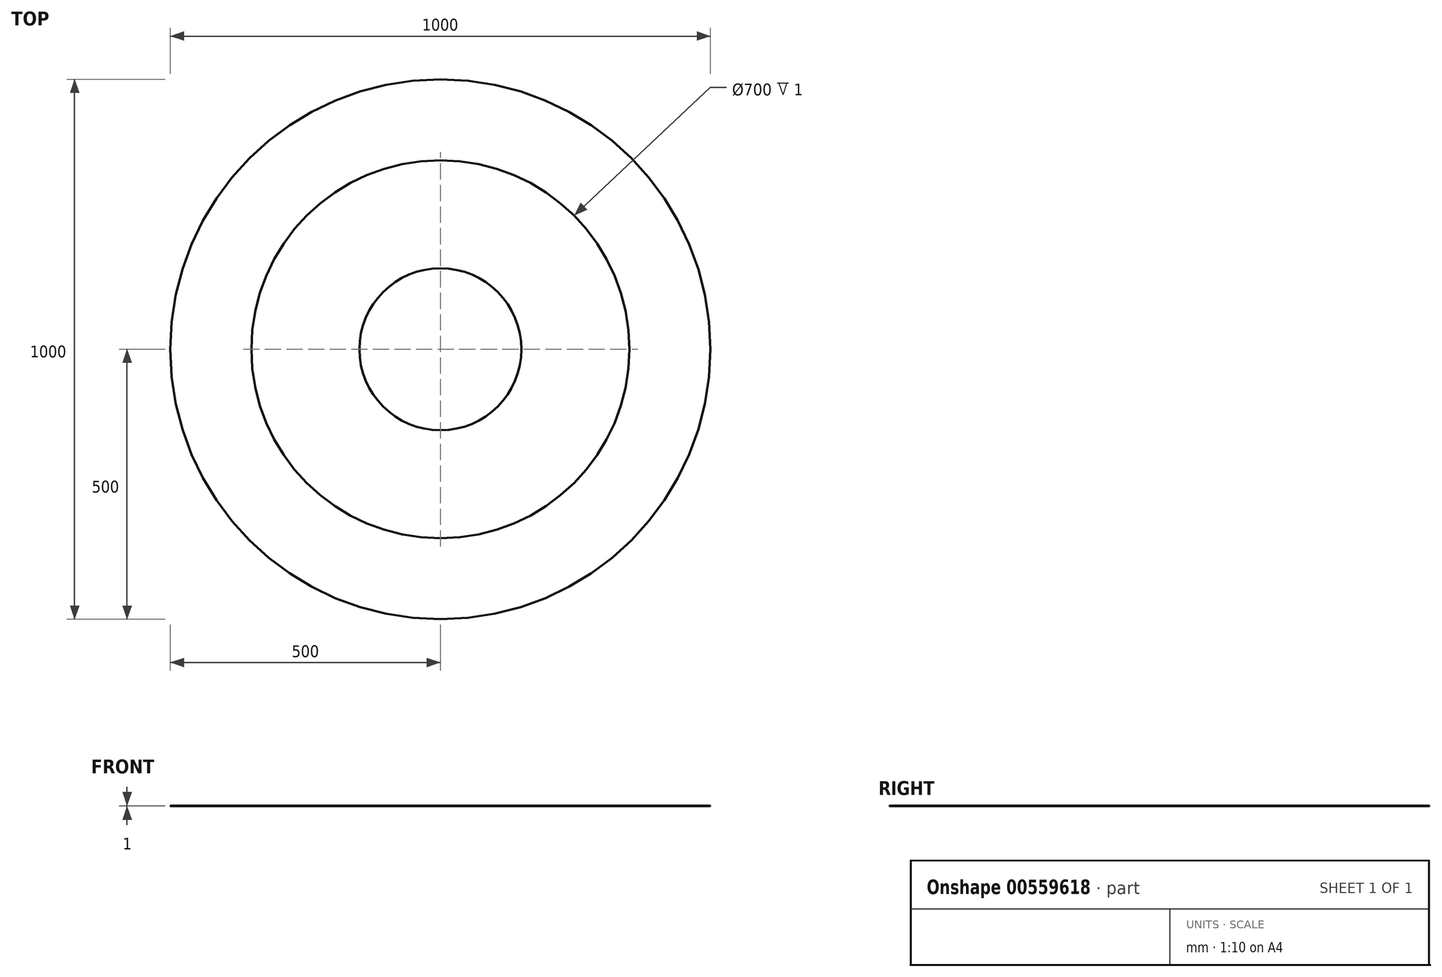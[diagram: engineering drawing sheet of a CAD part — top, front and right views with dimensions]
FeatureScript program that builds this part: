
annotation { "Feature Type Name" : "Feature", "Feature Type Description" : "" }
export const myFeature = defineFeature(function(context is Context, id is Id, definition is map)
    precondition{}
    {
        {
            var Q0;
            Q0=qCreatedBy(makeId("Top.planeOp"),FACE);
            var sketch = newSketch(context, id + "F0", { "sketchPlane" : qUnion([Q0])});
            skCircle(sketch, "E0", {"center": v(0, 0) * mm, "radius": 500 * mm});
            skCircle(sketch, "E1", {"center": v(0, 0) * mm, "radius": 350 * mm});
            skSolve(sketch);
        }
        {
            var Q0;
            Q0 = qSketchRegion(id + "F0", true);
            extrude(context, id + "F1", {"entities" : qUnion([Q0]), "depth" : 1 * mm, "offsetDistance" : 25.4 * mm});
        }
        {
            var Q0;
            Q0=qCreatedBy(makeId("Top.planeOp"),FACE);
            var sketch = newSketch(context, id + "F2", { "sketchPlane" : qUnion([Q0])});
            skCircle(sketch, "E2", {"center": v(0, 0) * mm, "radius": 150 * mm});
            skSolve(sketch);
        }
        {
            var Q0;
            Q0 = qSketchRegion(id + "F2", true);
            var Q1;
            Q1=makeQuery(id+"F1.opExtrude","CAP_FACE",FACE,{"disambiguationData":[OSD([sQuery(id+"F0.wireOp",EDGE,"E0"),sQuery(id+"F0.wireOp",EDGE,"E1")])],"isStart":false});
            extrude(context, id + "F3", {"entities" : qUnion([Q0]), "depth" : 1 * mm, "endBoundEntityFace" : qUnion([Q1]), "offsetDistance" : 25.4 * mm});
        }
    });
